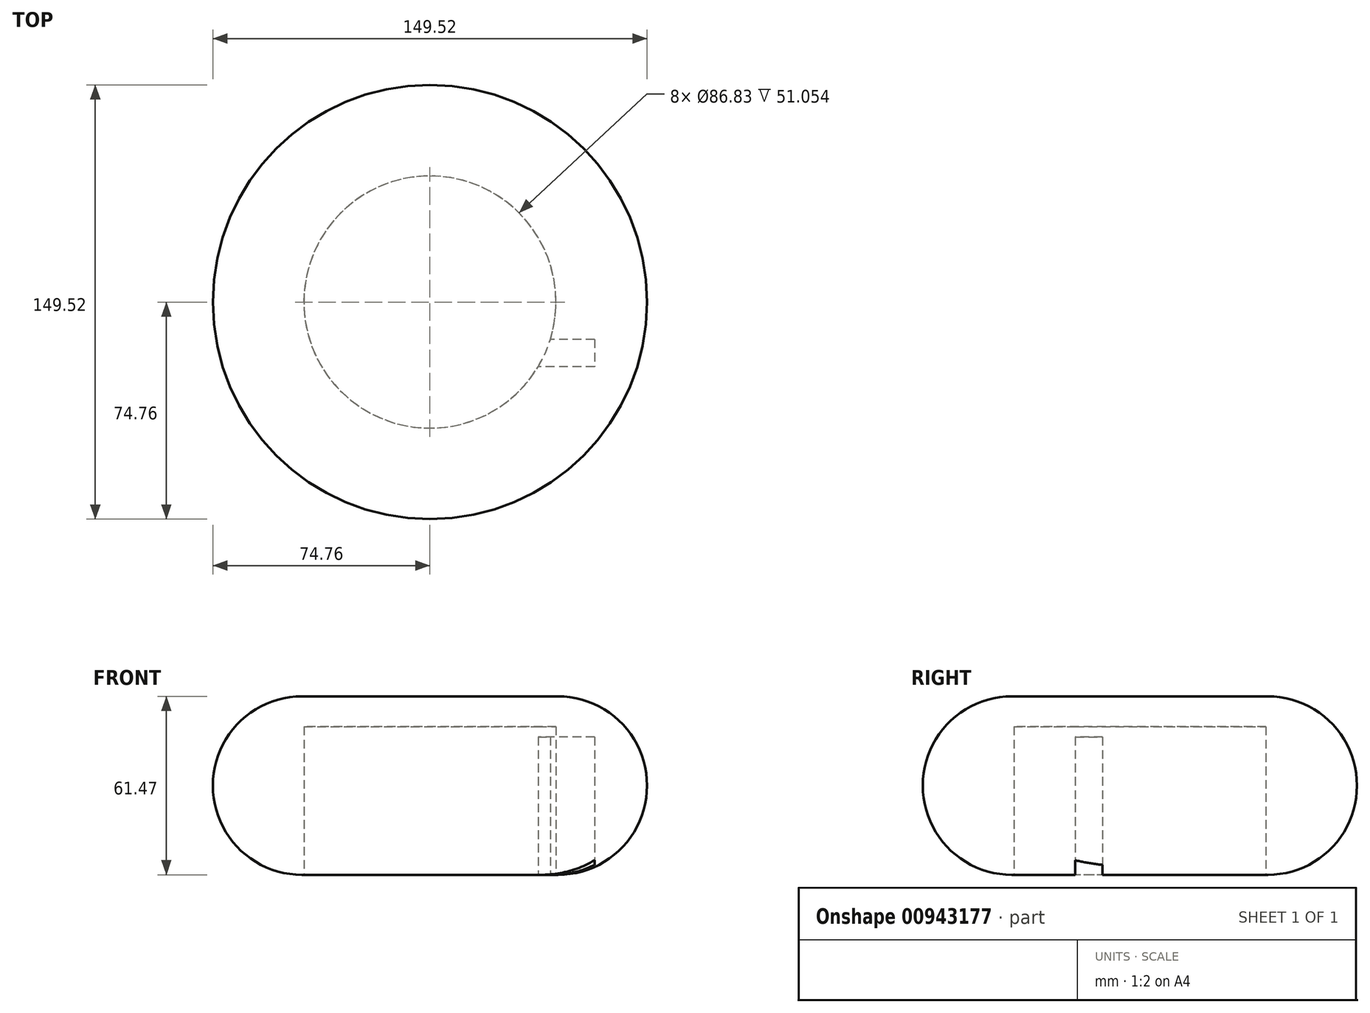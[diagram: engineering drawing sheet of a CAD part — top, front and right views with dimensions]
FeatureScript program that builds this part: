
annotation { "Feature Type Name" : "Feature", "Feature Type Description" : "" }
export const myFeature = defineFeature(function(context is Context, id is Id, definition is map)
    precondition{}
    {
        {
            var Q0;
            Q0=qCreatedBy(makeId("Top.planeOp"),FACE);
            var sketch = newSketch(context, id + "F0", { "sketchPlane" : qUnion([Q0])});
            skCircle(sketch, "E0", {"center": v(0, 0) * mm, "radius": 74.76 * mm});
            skSolve(sketch);
        }
        {
            var Q0;
            Q0=makeQuery(id+"F0.imprint","IMPRINT",FACE,{"disambiguationData":[TD([[makeQuery(id+"F0.imprint","IMPRINT",EDGE,{"derivedFrom":sQuery(id+"F0.wireOp",EDGE,"E0")}),1.0]])]});
            extrude(context, id + "F1", {"entities" : qUnion([Q0]), "depth" : 61.47 * mm, "offsetDistance" : 25.4 * mm});
        }
        {
            var Q0;
            Q0=qCreatedBy(makeId("Top.planeOp"),FACE);
            var sketch = newSketch(context, id + "F2", { "sketchPlane" : qUnion([Q0])});
            skCircle(sketch, "E1", {"center": v(0, 0) * mm, "radius": 43.41 * mm});
            skSolve(sketch);
        }
        {
            var Q0;
            Q0=makeQuery(id+"F2.imprint","IMPRINT",FACE,{"disambiguationData":[TD([[makeQuery(id+"F2.imprint","IMPRINT",EDGE,{"derivedFrom":sQuery(id+"F2.wireOp",EDGE,"E1")}),1.0]])]});
            extrude(context, id + "F3", {"entities" : qUnion([Q0]), "operationType" : NewBodyOperationType.REMOVE, "depth" : 51.05 * mm, "offsetDistance" : 25.4 * mm});
        }
        {
            var Q0;
            Q0=makeQuery(id+"F1.opExtrude","CAP_EDGE",EDGE,{"disambiguationData":[OSD([sQuery(id+"F0.wireOp",EDGE,"E0")])],"isStart":true});
            var Q1;
            Q1=makeQuery(id+"F1.opExtrude","CAP_EDGE",EDGE,{"disambiguationData":[OSD([sQuery(id+"F0.wireOp",EDGE,"E0")])],"isStart":false});
            fillet(context, id + "F4", {"entities" : qUnion([Q0, Q1]), "radius" : 30.66 * mm, "tangentPropagation" : true, "allowEdgeOverflow" : false});
        }
        {
            var Q0;
            Q0=qCreatedBy(makeId("Top.planeOp"),FACE);
            var sketch = newSketch(context, id + "F5", { "sketchPlane" : qUnion([Q0])});
            skLineSegment(sketch, "E2.bottom", {"start": v(56.7, -12.84) * mm, "end": v(20.16, -12.84) * mm});
            skLineSegment(sketch, "E2.top", {"start": v(56.7, -22.28) * mm, "end": v(20.16, -22.28) * mm});
            skLineSegment(sketch, "E2.left", {"start": v(56.7, -12.84) * mm, "end": v(56.7, -22.28) * mm});
            skLineSegment(sketch, "E2.right", {"start": v(20.16, -12.84) * mm, "end": v(20.16, -22.28) * mm});
            skSolve(sketch);
        }
        {
            var Q0;
            Q0=makeQuery(id+"F5.imprint","IMPRINT",FACE,{"disambiguationData":[TD([[makeQuery(id+"F5.imprint","IMPRINT",EDGE,{"derivedFrom":sQuery(id+"F5.wireOp",EDGE,"E2.bottom")}),1.0]])]});
            extrude(context, id + "F6", {"entities" : qUnion([Q0]), "operationType" : NewBodyOperationType.REMOVE, "depth" : 47.5 * mm, "offsetDistance" : 25.4 * mm});
        }
    });
